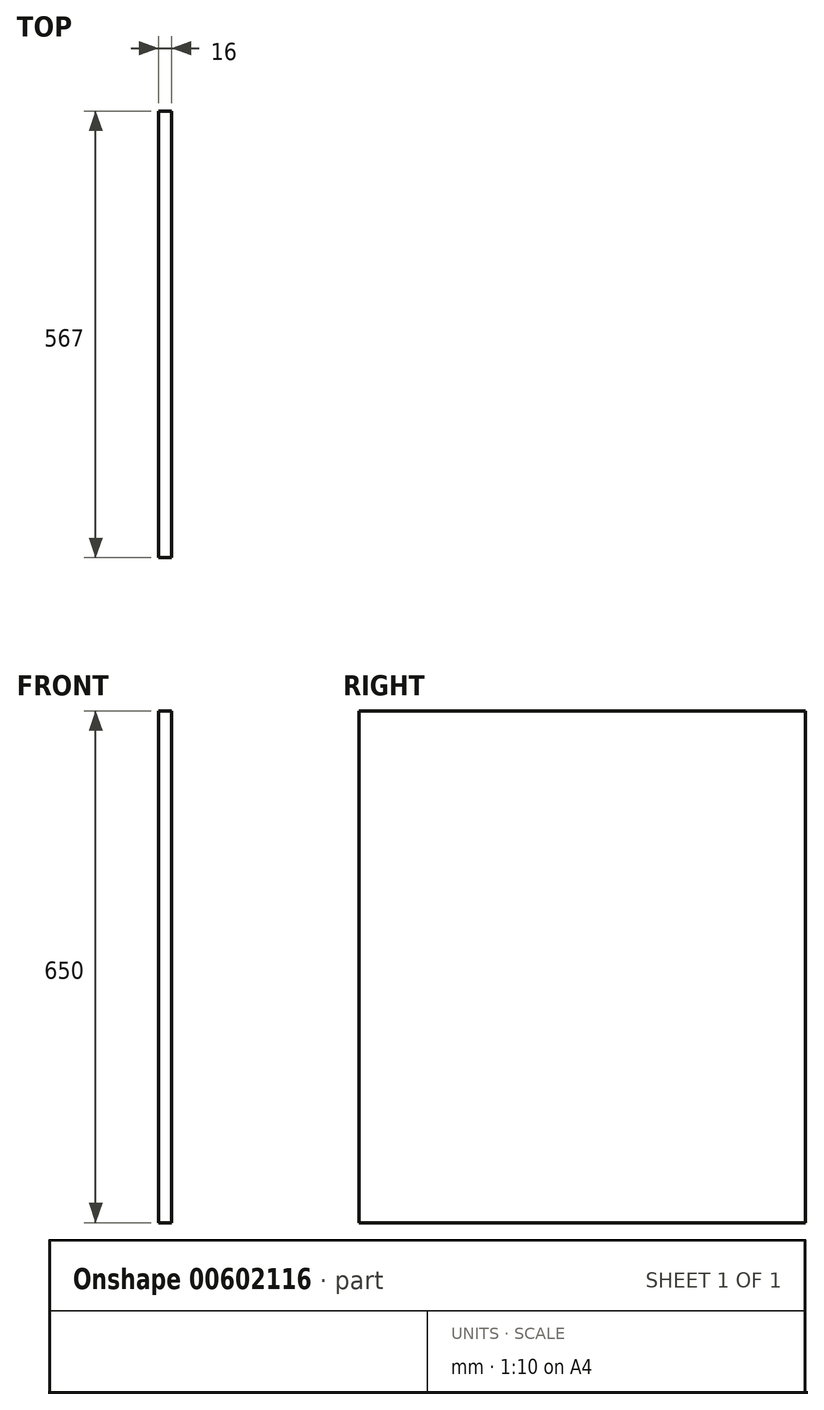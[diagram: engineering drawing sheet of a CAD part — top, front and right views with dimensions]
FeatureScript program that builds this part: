
annotation { "Feature Type Name" : "Feature", "Feature Type Description" : "" }
export const myFeature = defineFeature(function(context is Context, id is Id, definition is map)
    precondition{}
    {
        {
            var Q0;
            Q0=qCreatedBy(makeId("Right.planeOp"),FACE);
            var sketch = newSketch(context, id + "F0", { "sketchPlane" : qUnion([Q0])});
            skLineSegment(sketch, "E0.bottom", {"start": v(0, 0) * mm, "end": v(-567, 0) * mm});
            skLineSegment(sketch, "E0.top", {"start": v(0, 650) * mm, "end": v(-567, 650) * mm});
            skLineSegment(sketch, "E0.left", {"start": v(0, 0) * mm, "end": v(0, 650) * mm});
            skLineSegment(sketch, "E0.right", {"start": v(-567, 0) * mm, "end": v(-567, 650) * mm});
            skSolve(sketch);
        }
        {
            var Q0;
            Q0 = qSketchRegion(id + "F0", true);
            extrude(context, id + "F1", {"entities" : qUnion([Q0]), "depth" : 16 * mm, "offsetDistance" : 25 * mm});
        }
    });
